# Revit family: Haworth_BuzziCube_DuoPouf_EU_PRELIMINARY
name_source: partatom
category: Furniture
revit_build: Autodesk Revit 2018 (Build: 20170223_1515(x64)
units: mm (PartAtom-declared; Revit-internal decimal feet)

## family parameters
Always vertical = Yes
Cut with Voids When Loaded = No
OmniClass Number = 23.40.70.14.64.21
OmniClass Title = Systems Furniture
Room Calculation Point = No
Shared = No
Work Plane-Based = No

## types (4) — shared parameters
Actual Depth = 50 cm
Actual Height = 50 cm
Actual Width = 94 cm
Antiskid = Yes
Assembly Code = E2020200
Base Height Control = 1 cm
Base Width = 95 cm
Description = Haworth - BuzziCube - Duo Pouf
Manufacturer = Haworth
Model = P002X
Outer Offset = 22 cm
Revision Number = 1
Side Part Width = 45 cm
Size = Verify Final Dim. w/ Haworth
Square Offset = 2 cm
Square Pouf Width = 90 cm
URL = https://www.haworth.com
URL - Product = https://www.haworth.com
Warranty = http://www.haworth.com
Wood Base = No
Wood Finish = Haworth _ Wood _ Undecided

## per-type parameters (varying)
| type | 3D Visibility | Flat | Four Squares | One Square | Sixteen Squares |
| Duo - Flat | No | Yes | No | No | No |
| Duo - One Square | Yes | No | No | Yes | No |
| Duo - Four Squares | Yes | No | Yes | No | No |
| Duo - Sixteen Squares | Yes | No | No | No | Yes |

## geometry (parser evidence)
native form markers: Sweep x13
no freeform markers — native parametric forms only
